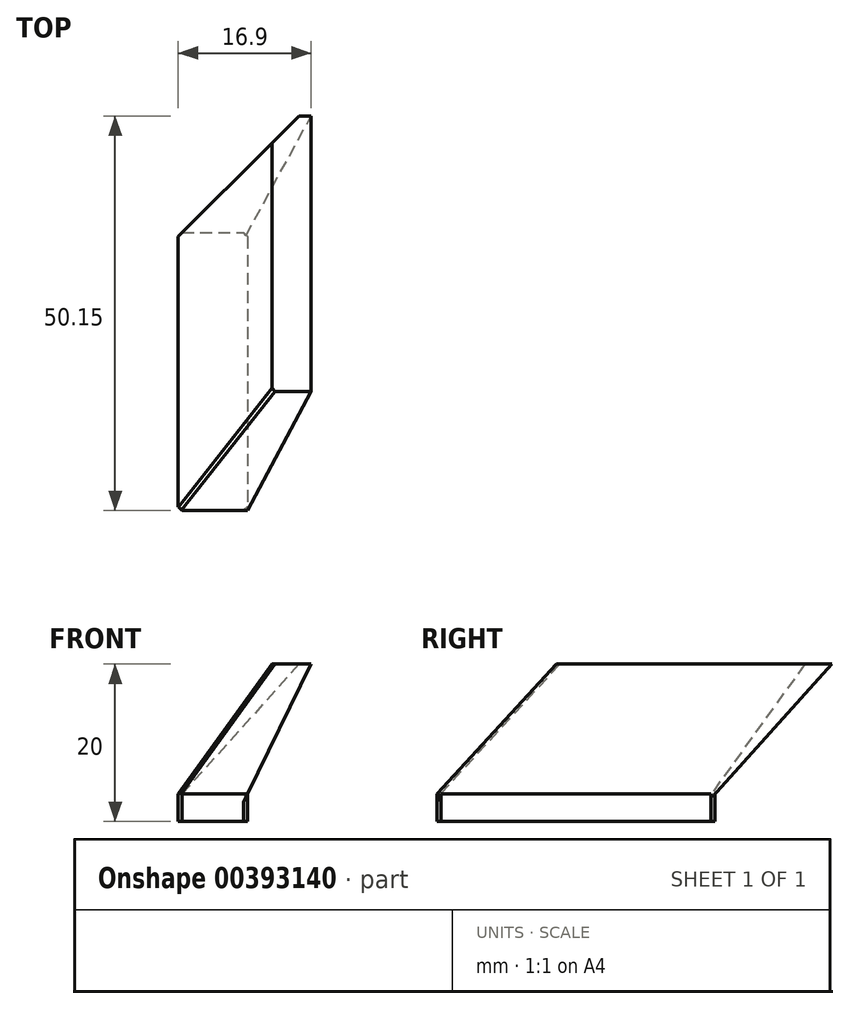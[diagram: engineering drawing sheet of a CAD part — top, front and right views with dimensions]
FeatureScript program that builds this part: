
annotation { "Feature Type Name" : "Feature", "Feature Type Description" : "" }
export const myFeature = defineFeature(function(context is Context, id is Id, definition is map)
    precondition{}
    {
        {
            assignVariable(context, id + "F0", {"variableType" : VariableType.LENGTH, "name" : "zoff", "lengthValue" : 16.5 * mm});
        }
        {
            var Q0;
            Q0=qCreatedBy(makeId("Top.planeOp"),FACE);
            var sketch = newSketch(context, id + "F1", { "sketchPlane" : qUnion([Q0])});
            skLineSegment(sketch, "E0.bottom", {"start": v(4.4, 17.65) * mm, "end": v(-4.4, 17.65) * mm});
            skLineSegment(sketch, "E0.top", {"start": v(4.4, -17.65) * mm, "end": v(-4.4, -17.65) * mm});
            skLineSegment(sketch, "E0.left", {"start": v(4.4, 17.65) * mm, "end": v(4.4, -17.65) * mm});
            skLineSegment(sketch, "E0.right", {"start": v(-4.4, 17.65) * mm, "end": v(-4.4, -17.65) * mm});
            skPoint(sketch, "E0.middle", {"position": v(0, 0) * mm});
            skSolve(sketch);
        }
        {
            var Q0;
            Q0=qCreatedBy(makeId("Top.planeOp"),FACE);
            cPlane(context, id + "F2", {"entities" : qUnion([Q0]), "cplaneType" : CPlaneType.OFFSET, "offset" : getVariable(context, 'zoff'), "oppositeDirection" : true, "width" : 150 * mm, "height" : 150 * mm});
        }
        {
            var Q0;
            Q0=qCreatedBy(id+"F2.planeOp",FACE);
            var sketch = newSketch(context, id + "F3", { "sketchPlane" : qUnion([Q0])});
            skLineSegment(sketch, "E1.bottom", {"start": v(-7.5, 32.5) * mm, "end": v(-12.5, 32.5) * mm});
            skLineSegment(sketch, "E1.top", {"start": v(-7.5, -2.5) * mm, "end": v(-12.5, -2.5) * mm});
            skLineSegment(sketch, "E1.left", {"start": v(-7.5, 32.5) * mm, "end": v(-7.5, -2.5) * mm});
            skLineSegment(sketch, "E1.right", {"start": v(-12.5, 32.5) * mm, "end": v(-12.5, -2.5) * mm});
            skPoint(sketch, "E1.middle", {"position": v(-10, 15) * mm});
            skSolve(sketch);
        }
        {
            var Q0;
            Q0=makeQuery(id+"F1.imprint","IMPRINT",FACE,{"disambiguationData":[TD([[makeQuery(id+"F1.imprint","IMPRINT",EDGE,{"derivedFrom":sQuery(id+"F1.wireOp",EDGE,"E0.bottom")}),1.0]])]});
            extrude(context, id + "F4", {"entities" : qUnion([Q0]), "depth" : 3.5 * mm, "offsetDistance" : 25 * mm});
        }
        {
            var Q0;
            Q0=makeQuery(id+"F4.opExtrude","CAP_FACE",FACE,{"disambiguationData":[OSD([sQuery(id+"F1.wireOp",EDGE,"E0.bottom"),sQuery(id+"F1.wireOp",EDGE,"E0.top"),sQuery(id+"F1.wireOp",EDGE,"E0.left"),sQuery(id+"F1.wireOp",EDGE,"E0.right")])],"isStart":true});
            var Q1;
            Q1=makeQuery(id+"F3.imprint","IMPRINT",FACE,{"disambiguationData":[TD([[makeQuery(id+"F3.imprint","IMPRINT",EDGE,{"derivedFrom":sQuery(id+"F3.wireOp",EDGE,"E1.bottom")}),1.0]])]});
            loft(context, id + "F5", {"operationType" : NewBodyOperationType.ADD, "sheetProfilesArray" : [{ "sheetProfileEntities" : qUnion([Q0]) }, { "sheetProfileEntities" : qUnion([Q1]) }]});
        }
        {
            var Q0;
            Q0=makeQuery(id+"F4.opExtrude","SWEPT_BODY",BODY,{"disambiguationData":[OSD([sQuery(id+"F1.wireOp",EDGE,"E0.bottom"),sQuery(id+"F1.wireOp",EDGE,"E0.top"),sQuery(id+"F1.wireOp",EDGE,"E0.left"),sQuery(id+"F1.wireOp",EDGE,"E0.right")])]});
            var Q1;
            Q1=makeQuery(id+"F4.opExtrude","CAP_EDGE",EDGE,{"disambiguationData":[OSD([sQuery(id+"F1.wireOp",EDGE,"E0.right")])],"isStart":false});
            transform(context, id + "F6", {"entities" : qUnion([Q0]), "transformType" : TransformType.ROTATION, "transformAxis" : qUnion([Q1]), "angle" : 180 * degree, "makeCopy" : false});
        }
        {
            var Q0;
            Q0=makeQuery(id+"F4.opExtrude","SWEPT_EDGE",EDGE,{"disambiguationData":[OSD([sQuery(id+"F1.wireOp",EDGE,"E0.bottom"),sQuery(id+"F1.wireOp",EDGE,"E0.right")])]});
            var Q1;
            Q1=makeQuery(id+"F4.opExtrude","SWEPT_EDGE",EDGE,{"disambiguationData":[OSD([sQuery(id+"F1.wireOp",EDGE,"E0.bottom"),sQuery(id+"F1.wireOp",EDGE,"E0.left")])]});
            var Q2;
            Q2=makeQuery(id+"F4.opExtrude","SWEPT_EDGE",EDGE,{"disambiguationData":[OSD([sQuery(id+"F1.wireOp",EDGE,"E0.top"),sQuery(id+"F1.wireOp",EDGE,"E0.left")])]});
            var Q3;
            Q3=makeQuery(id+"F4.opExtrude","SWEPT_EDGE",EDGE,{"disambiguationData":[OSD([sQuery(id+"F1.wireOp",EDGE,"E0.top"),sQuery(id+"F1.wireOp",EDGE,"E0.right")])]});
            var Q4;
            Q4=makeQuery(id+"F5.opLoft","SWEPT_EDGE",EDGE,{"disambiguationData":[OSD([sQuery(id+"F1.wireOp",EDGE,"E0.top"),sQuery(id+"F1.wireOp",EDGE,"E0.left"),sQuery(id+"F3.wireOp",EDGE,"E1.top"),sQuery(id+"F3.wireOp",EDGE,"E1.left")])]});
            chamfer(context, id + "F7", {"entities" : qUnion([Q0, Q1, Q2, Q3, Q4]), "width" : 0.5 * mm, "tangentPropagation" : true});
        }
    });
